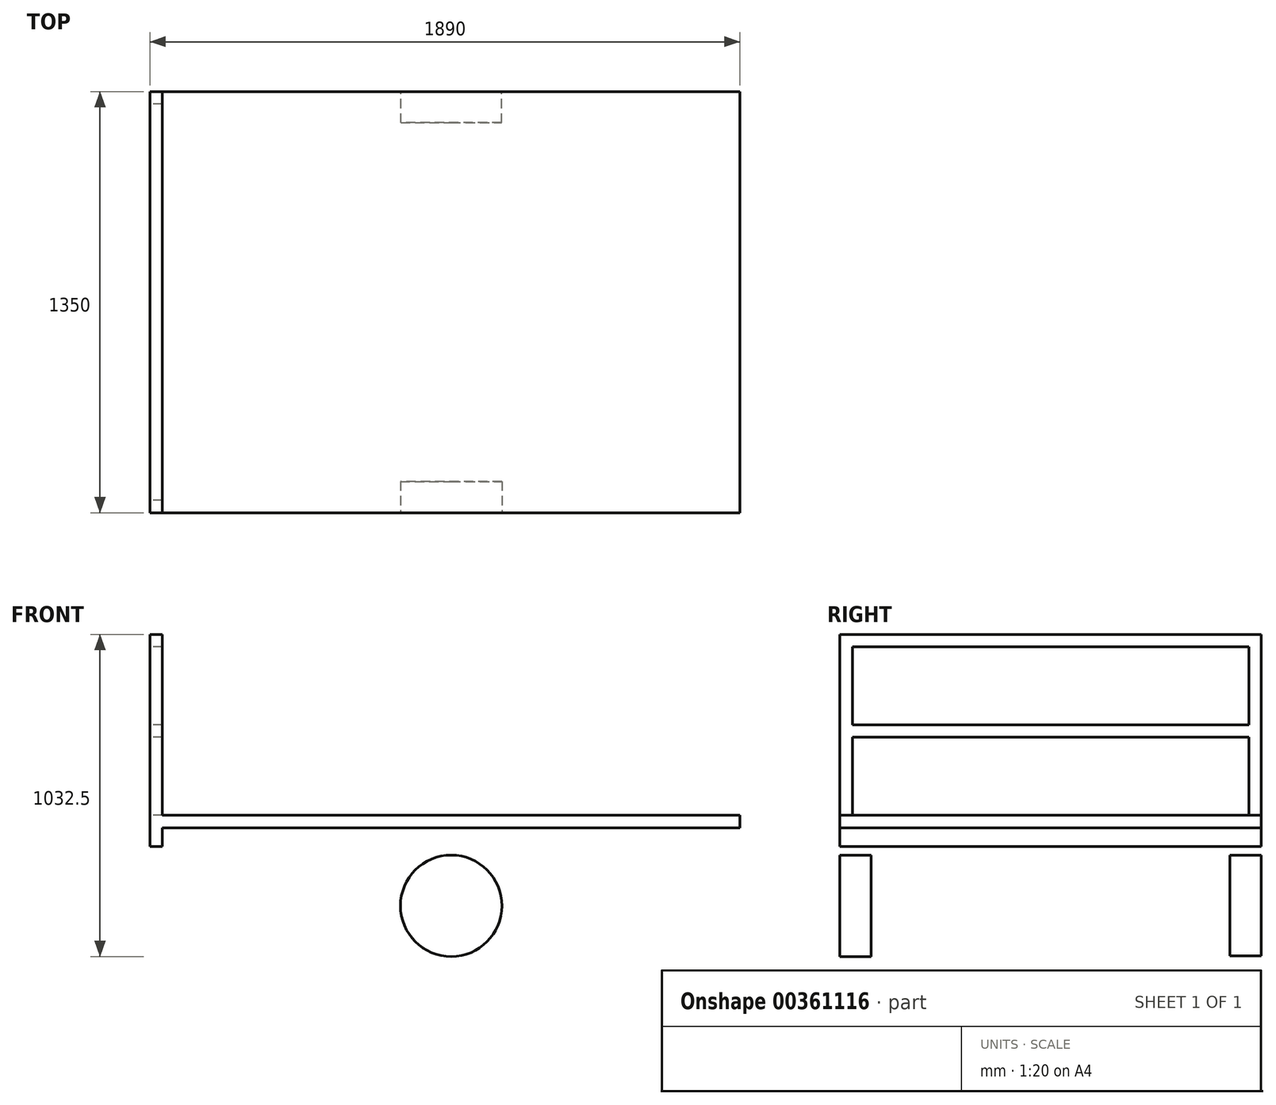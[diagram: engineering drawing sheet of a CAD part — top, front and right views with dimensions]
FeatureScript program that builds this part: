
annotation { "Feature Type Name" : "Feature", "Feature Type Description" : "" }
export const myFeature = defineFeature(function(context is Context, id is Id, definition is map)
    precondition{}
    {
        {
            var Q0;
            Q0=qCreatedBy(makeId("Top.planeOp"),FACE);
            var sketch = newSketch(context, id + "F0", { "sketchPlane" : qUnion([Q0])});
            skLineSegment(sketch, "E0.bottom", {"start": v(0, 0) * mm, "end": v(1850, 0) * mm});
            skLineSegment(sketch, "E0.top", {"start": v(0, 1350) * mm, "end": v(1850, 1350) * mm});
            skLineSegment(sketch, "E0.left", {"start": v(0, 0) * mm, "end": v(0, 1350) * mm});
            skLineSegment(sketch, "E0.right", {"start": v(1850, 0) * mm, "end": v(1850, 1350) * mm});
            skSolve(sketch);
        }
        {
            var Q0;
            Q0=makeQuery(id+"F0.imprint","IMPRINT",FACE,{"disambiguationData":[TD([[makeQuery(id+"F0.imprint","IMPRINT",EDGE,{"derivedFrom":sQuery(id+"F0.wireOp",EDGE,"E0.bottom")}),1.0]])]});
            extrude(context, id + "F1", {"entities" : qUnion([Q0]), "oppositeDirection" : true, "depth" : 40 * mm});
        }
        {
            var Q0;
            Q0=qCreatedBy(makeId("Top.planeOp"),FACE);
            var sketch = newSketch(context, id + "F2", { "sketchPlane" : qUnion([Q0])});
            skLineSegment(sketch, "E1.bottom", {"start": v(0, 0) * mm, "end": v(-40, 0) * mm});
            skLineSegment(sketch, "E1.top", {"start": v(0, 1350) * mm, "end": v(-40, 1350) * mm});
            skLineSegment(sketch, "E1.left", {"start": v(0, 0) * mm, "end": v(0, 1350) * mm});
            skLineSegment(sketch, "E1.right", {"start": v(-40, 0) * mm, "end": v(-40, 1350) * mm});
            skSolve(sketch);
        }
        {
            var Q0;
            Q0=makeQuery(id+"F2.imprint","IMPRINT",FACE,{"disambiguationData":[TD([[makeQuery(id+"F2.imprint","IMPRINT",EDGE,{"derivedFrom":sQuery(id+"F2.wireOp",EDGE,"E1.bottom")}),-1.0]])]});
            extrude(context, id + "F3", {"entities" : qUnion([Q0]), "operationType" : NewBodyOperationType.ADD, "oppositeDirection" : true, "depth" : 100 * mm, "hasSecondDirection" : true, "secondDirectionOppositeDirection" : false, "secondDirectionDepth" : 580 * mm});
        }
        {
            var Q0;
            Q0=makeQuery(id+"F3.boolean.opBoolean","MERGE",FACE,{"derivedFrom":[makeQuery(id+"F1.opExtrude","SWEPT_FACE",FACE,{"disambiguationData":[OSD([sQuery(id+"F0.wireOp",EDGE,"E0.bottom")])]}),makeQuery(id+"F3.opExtrude","SWEPT_FACE",FACE,{"disambiguationData":[OSD([sQuery(id+"F2.wireOp",EDGE,"E1.bottom")])]})]});
            var sketch = newSketch(context, id + "F4", { "sketchPlane" : qUnion([Q0])});
            skLineSegment(sketch, "E2", {"start": v(925, -40) * mm, "end": v(925, -290) * mm, "construction": true});
            skCircle(sketch, "E3", {"center": v(925, -290) * mm, "radius": 162.5 * mm});
            skSolve(sketch);
        }
        {
            var Q0;
            Q0=makeQuery(id+"F4.imprint","IMPRINT",FACE,{"disambiguationData":[TD([[makeQuery(id+"F4.imprint","IMPRINT",EDGE,{"derivedFrom":sQuery(id+"F4.wireOp",EDGE,"E3")}),1.0]])]});
            extrude(context, id + "F5", {"entities" : qUnion([Q0]), "oppositeDirection" : true, "depth" : 100 * mm});
        }
        {
            var Q0;
            Q0=makeQuery(id+"F3.boolean.opBoolean","MERGE",FACE,{"derivedFrom":[makeQuery(id+"F1.opExtrude","SWEPT_FACE",FACE,{"disambiguationData":[OSD([sQuery(id+"F0.wireOp",EDGE,"E0.top")])]}),makeQuery(id+"F3.opExtrude","SWEPT_FACE",FACE,{"disambiguationData":[OSD([sQuery(id+"F2.wireOp",EDGE,"E1.top")])]})]});
            var sketch = newSketch(context, id + "F6", { "sketchPlane" : qUnion([Q0])});
            skLineSegment(sketch, "E4", {"start": v(-925, -40) * mm, "end": v(-925, -289.1) * mm, "construction": true});
            skCircle(sketch, "E5", {"center": v(-925, -289.1) * mm, "radius": 161.32 * mm});
            skSolve(sketch);
        }
        {
            var Q0;
            Q0=makeQuery(id+"F6.imprint","IMPRINT",FACE,{"disambiguationData":[TD([[makeQuery(id+"F6.imprint","IMPRINT",EDGE,{"derivedFrom":sQuery(id+"F6.wireOp",EDGE,"E5")}),1.0]])]});
            extrude(context, id + "F7", {"entities" : qUnion([Q0]), "oppositeDirection" : true, "depth" : 100 * mm});
        }
        {
            var Q0;
            Q0=makeQuery(id+"F3.opExtrude","SWEPT_FACE",FACE,{"disambiguationData":[OSD([sQuery(id+"F2.wireOp",EDGE,"E1.right")])]});
            var sketch = newSketch(context, id + "F8", { "sketchPlane" : qUnion([Q0])});
            skLineSegment(sketch, "E6", {"start": v(0, 0) * mm, "end": v(-40.2, 0) * mm, "construction": true});
            skLineSegment(sketch, "E7", {"start": v(-40.2, 0) * mm, "end": v(-1350, 0) * mm, "construction": true});
            skLineSegment(sketch, "E8", {"start": v(-1350, 0) * mm, "end": v(-1310.17, 0) * mm, "construction": true});
            skLineSegment(sketch, "E9", {"start": v(-1310.17, 0) * mm, "end": v(-1310.17, 250) * mm, "construction": true});
            skLineSegment(sketch, "E10", {"start": v(-1310.17, 250) * mm, "end": v(-40.2, 250) * mm, "construction": true});
            skLineSegment(sketch, "E11", {"start": v(-40.2, 250) * mm, "end": v(-40.2, 290) * mm});
            skLineSegment(sketch, "E12", {"start": v(-40.2, 290) * mm, "end": v(-1310.17, 290) * mm});
            skLineSegment(sketch, "E13", {"start": v(-1310.17, 290) * mm, "end": v(-1310.17, 540) * mm});
            skLineSegment(sketch, "E14.bottom", {"start": v(-1310.17, 540) * mm, "end": v(-40.2, 540) * mm});
            skLineSegment(sketch, "E14.top", {"start": v(-1310.17, 290) * mm, "end": v(-40.2, 290) * mm});
            skLineSegment(sketch, "E14.left", {"start": v(-1310.17, 540) * mm, "end": v(-1310.17, 290) * mm});
            skLineSegment(sketch, "E14.right", {"start": v(-40.2, 540) * mm, "end": v(-40.2, 290) * mm});
            skLineSegment(sketch, "E15.bottom", {"start": v(-1310.17, 250) * mm, "end": v(-40.2, 250) * mm});
            skLineSegment(sketch, "E15.top", {"start": v(-1310.17, 0) * mm, "end": v(-40.2, 0) * mm});
            skLineSegment(sketch, "E15.left", {"start": v(-1310.17, 250) * mm, "end": v(-1310.17, 0) * mm});
            skLineSegment(sketch, "E15.right", {"start": v(-40.2, 250) * mm, "end": v(-40.2, 0) * mm});
            skSolve(sketch);
        }
        {
            var Q0;
            Q0=makeQuery(id+"F8.imprint","IMPRINT",FACE,{"disambiguationData":[TD([[makeQuery(id+"F8.imprint","IMPRINT",EDGE,{"derivedFrom":sQuery(id+"F8.wireOp",EDGE,"E14.bottom")}),-1.0]])]});
            extrude(context, id + "F9", {"entities" : qUnion([Q0]), "operationType" : NewBodyOperationType.REMOVE, "oppositeDirection" : true, "depth" : 100 * mm});
        }
        {
            var Q0;
            Q0 = qSketchRegion(id + "F8", true);
            extrude(context, id + "F10", {"entities" : qUnion([Q0]), "operationType" : NewBodyOperationType.REMOVE, "oppositeDirection" : true, "depth" : 100 * mm});
        }
    });
